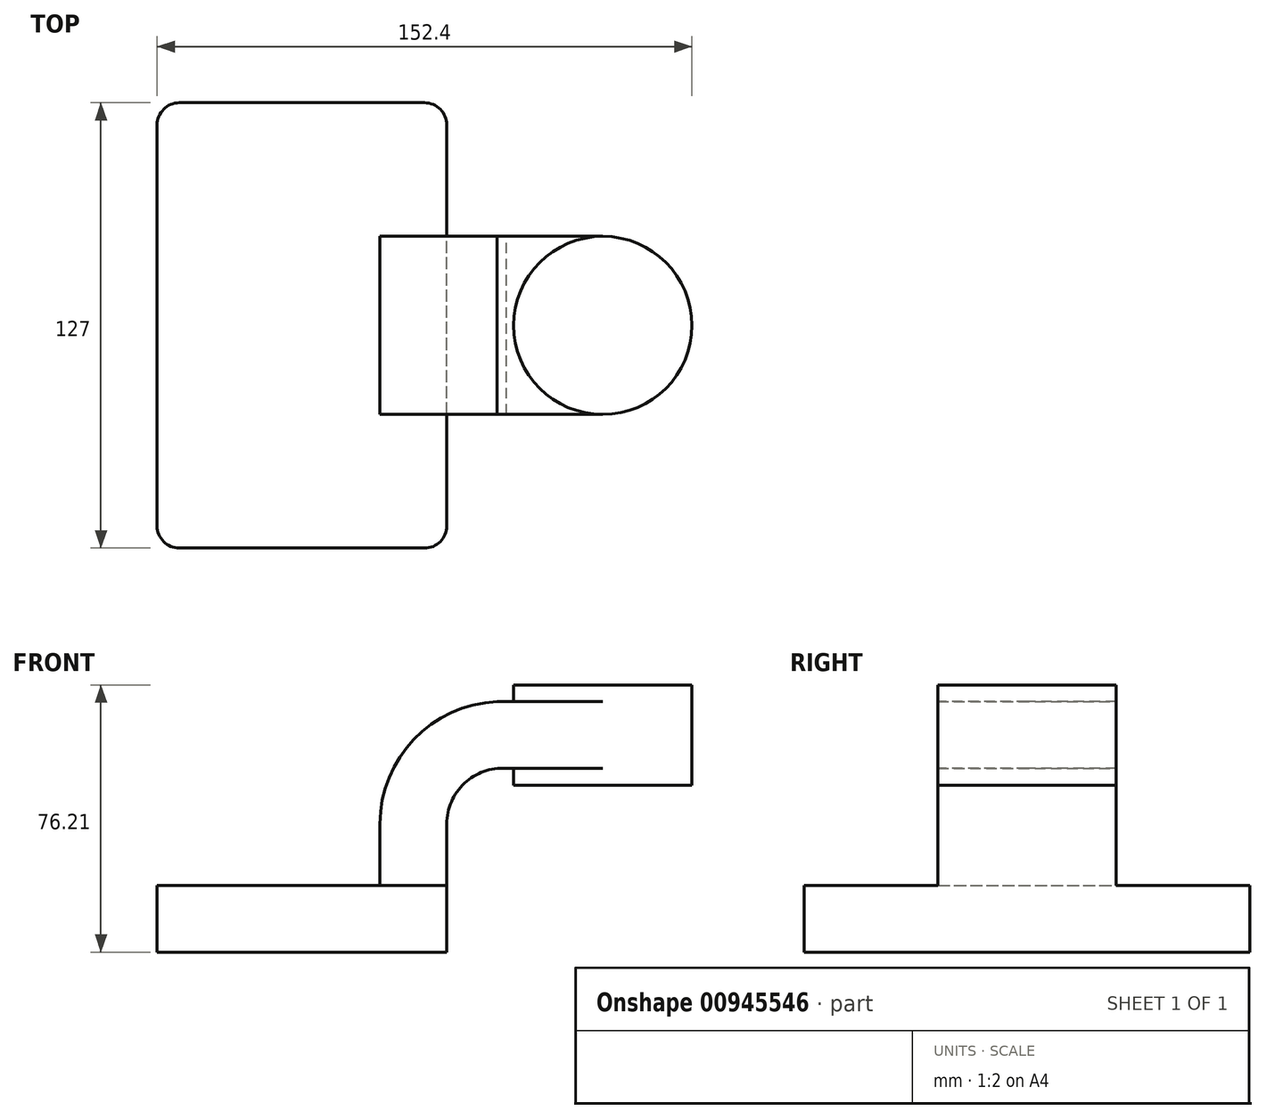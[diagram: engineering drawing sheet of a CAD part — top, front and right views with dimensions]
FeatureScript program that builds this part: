
annotation { "Feature Type Name" : "Feature", "Feature Type Description" : "" }
export const myFeature = defineFeature(function(context is Context, id is Id, definition is map)
    precondition{}
    {
        {
            var Q0;
            Q0=qCreatedBy(makeId("Front.planeOp"),FACE);
            var sketch = newSketch(context, id + "F0", { "sketchPlane" : qUnion([Q0])});
            skLineSegment(sketch, "E0.bottom", {"start": v(-41.28, -9.53) * mm, "end": v(41.28, -9.53) * mm});
            skLineSegment(sketch, "E0.top", {"start": v(-41.28, 9.53) * mm, "end": v(41.28, 9.53) * mm});
            skLineSegment(sketch, "E0.left", {"start": v(-41.28, -9.53) * mm, "end": v(-41.28, 9.53) * mm});
            skLineSegment(sketch, "E0.right", {"start": v(41.28, -9.53) * mm, "end": v(41.28, 9.52) * mm});
            skPoint(sketch, "E0.middle", {"position": v(0, 0) * mm});
            skLineSegment(sketch, "E1.bottom", {"start": v(60.32, 38.1) * mm, "end": v(111.12, 38.1) * mm});
            skLineSegment(sketch, "E1.top", {"start": v(60.32, 66.67) * mm, "end": v(111.12, 66.67) * mm});
            skLineSegment(sketch, "E1.left", {"start": v(60.32, 38.1) * mm, "end": v(60.32, 66.67) * mm});
            skLineSegment(sketch, "E1.right", {"start": v(111.12, 38.1) * mm, "end": v(111.12, 66.67) * mm});
            skPoint(sketch, "E1.middle", {"position": v(85.72, 52.39) * mm});
            skLineSegment(sketch, "E2", {"start": v(41.28, 9.52) * mm, "end": v(41.28, 27.04) * mm});
            skArc(sketch, "E3", {"start": v(41.28, 27.04) * mm, "mid": v(46.31, 38.63) * mm, "end": v(58.22, 42.88) * mm});
            skLineSegment(sketch, "E4", {"start": v(58.22, 42.88) * mm, "end": v(85.72, 42.88) * mm});
            skLineSegment(sketch, "E5.0", {"start": v(55.56, 61.93) * mm, "end": v(85.72, 61.93) * mm});
            skArc(sketch, "E5.1", {"start": v(22.23, 27.04) * mm, "mid": v(31.9, 51.16) * mm, "end": v(55.56, 61.93) * mm});
            skLineSegment(sketch, "E5.2", {"start": v(22.22, 9.52) * mm, "end": v(22.22, 27.04) * mm});
            skFitSpline(sketch, "E6", {"points": [v(-41.28, 9.53) * mm, v(55.56, 61.93) * mm], "startDerivative": vector(1.7, 63.03) * mm, "endDerivative": vector(111.72, 1.38) * mm});
            skLineSegment(sketch, "E7", {"start": v(85.72, 38.1) * mm, "end": v(85.72, 66.67) * mm});
            skSolve(sketch);
        }
        {
            var Q0;
            Q0=makeQuery(id+"F0.imprint","IMPRINT",FACE,{"disambiguationData":[TD([[makeQuery(id+"F0.imprint","IMPRINT",EDGE,{"derivedFrom":sQuery(id+"F0.wireOp",EDGE,"E0.bottom")}),1.0]])]});
            var Q1;
            Q1=sQuery(id+"F0.wireOp",EDGE,"E6");
            extrude(context, id + "F1", {"entities" : qUnion([Q0]), "surfaceEntities" : qUnion([Q1]), "endBound" : BoundingType.SYMMETRIC, "depth" : 127 * mm, "offsetDistance" : 25.4 * mm});
        }
        {
            var Q0;
            {var subQ1=sQuery(id+"F0.wireOp",EDGE,"E2");Q0=makeQuery(id+"F0.imprint","IMPRINT",FACE,{"disambiguationData":[TD([[makeQuery(id+"F0.imprint","IMPRINT",EDGE,{"derivedFrom":subQ1}),1.0]])]});}
            var Q1;
            {var subQ0=sQuery(id+"F0.wireOp",EDGE,"E4");var subQ1=sQuery(id+"F0.wireOp",EDGE,"E1.left");var subQ2=makeQuery(id+"F0.imprint","INTERSECT",VERTEX,{"derivedFrom":[subQ1,subQ0]});Q1=makeQuery(id+"F0.imprint","IMPRINT",FACE,{"disambiguationData":[TD([[makeQuery(id+"F0.imprint","IMPRINT",EDGE,{"disambiguationData":[TD([[subQ2,-1.0]])],"derivedFrom":subQ1}),-1.0]])]});}
            extrude(context, id + "F2", {"entities" : qUnion([Q0, Q1]), "operationType" : NewBodyOperationType.ADD, "endBound" : BoundingType.SYMMETRIC, "depth" : 50.8 * mm, "offsetDistance" : 25.4 * mm});
        }
        {
            var Q0;
            Q0=makeQuery(id+"F0.imprint","IMPRINT",FACE,{"disambiguationData":[TD([[makeQuery(id+"F0.imprint","IMPRINT",EDGE,{"derivedFrom":sQuery(id+"F0.wireOp",EDGE,"E5.1")}),1.0]])]});
            extrude(context, id + "F3", {"entities" : qUnion([Q0]), "operationType" : NewBodyOperationType.ADD, "endBound" : BoundingType.SYMMETRIC, "depth" : 15.88 * mm, "offsetDistance" : 25.4 * mm});
        }
        {
            var Q0;
            {var subQ4=sQuery(id+"F0.wireOp",EDGE,"E1.right");Q0=makeQuery(id+"F0.imprint","IMPRINT",FACE,{"disambiguationData":[TD([[makeQuery(id+"F0.imprint","IMPRINT",EDGE,{"derivedFrom":subQ4}),1.0]])]});}
            var Q1;
            Q1=sQuery(id+"F0.wireOp",EDGE,"E7");
            revolve(context, id + "F4", {"operationType" : NewBodyOperationType.ADD, "surfaceOperationType" : NewSurfaceOperationType.NEW, "entities" : qUnion([Q0]), "axis" : qUnion([Q1]), "revolveType" : RevolveType.FULL});
        }
        {
            var Q0;
            Q0=makeQuery(id+"F1.opExtrude","CAP_EDGE",EDGE,{"disambiguationData":[OSD([sQuery(id+"F0.wireOp",EDGE,"E0.right")])],"isStart":false});
            var Q1;
            Q1=makeQuery(id+"F1.opExtrude","CAP_EDGE",EDGE,{"disambiguationData":[OSD([sQuery(id+"F0.wireOp",EDGE,"E0.left")])],"isStart":false});
            var Q2;
            Q2=makeQuery(id+"F1.opExtrude","CAP_EDGE",EDGE,{"disambiguationData":[OSD([sQuery(id+"F0.wireOp",EDGE,"E0.left")])],"isStart":true});
            var Q3;
            Q3=makeQuery(id+"F1.opExtrude","CAP_EDGE",EDGE,{"disambiguationData":[OSD([sQuery(id+"F0.wireOp",EDGE,"E0.right")])],"isStart":true});
            fillet(context, id + "F5", {"entities" : qUnion([Q0, Q1, Q2, Q3]), "radius" : 6.35 * mm, "tangentPropagation" : true, "allowEdgeOverflow" : false});
        }
    });
